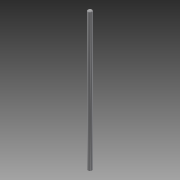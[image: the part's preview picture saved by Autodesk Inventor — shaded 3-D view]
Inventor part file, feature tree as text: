
AUTODESK INVENTOR PART (.ipt)
format: ipt  version: 2015 (Build 190159000, 159)  size: 78,336 bytes
history: native  units: mm
features: sketch x3, extrude x1, chamfer x1
ambient origin geometry x8: Origin, YZ Plane, XZ Plane, XY Plane, X Axis, Y Axis, Z Axis, Center Point
bodies: Solid1 (feature_tree)
feature tree (5):
  sketch  "Sketch1"  dims[d1=6.0mm d2=200.0mm d3=0.0mm d4=0.5mm d5=2.0mm d6=45.0deg]
  sketch  "Sketch2"
  extrude  "Extrusion1"  Depth=200.0mm TaperAngle=0.0deg
  sketch  "Sketch3"
  chamfer  "Chamfer1"  Distance=0.5mm Angle=45.0deg
